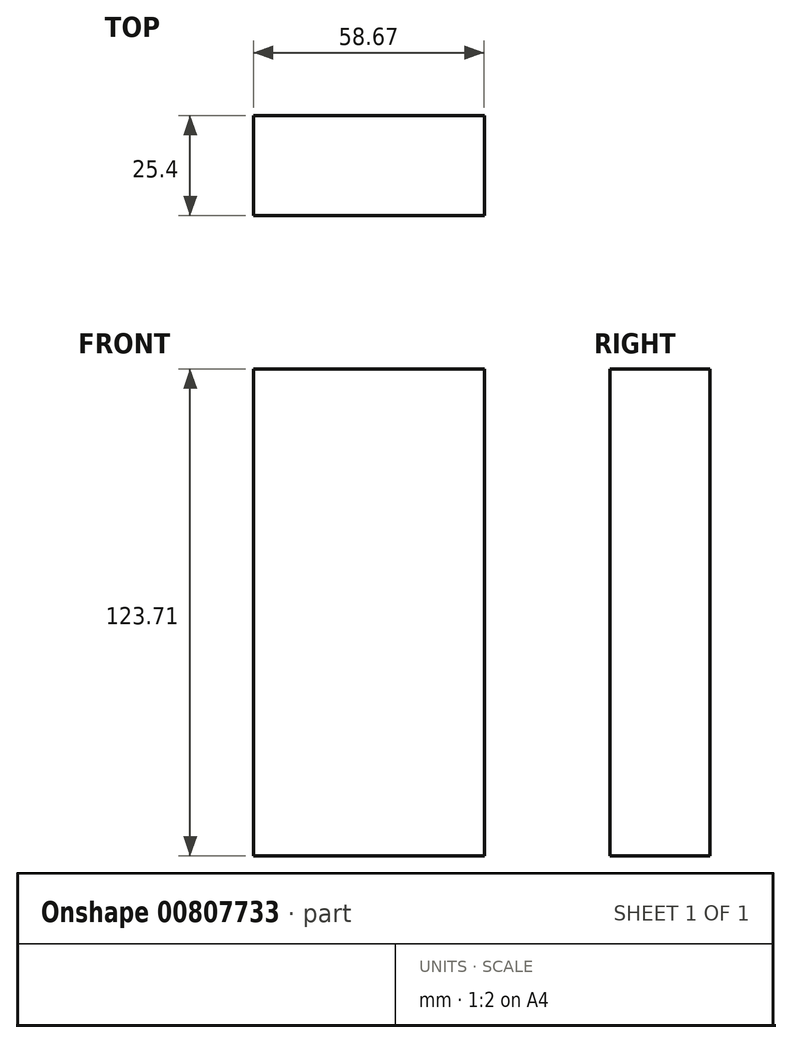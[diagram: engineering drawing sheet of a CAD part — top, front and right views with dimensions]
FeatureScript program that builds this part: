
annotation { "Feature Type Name" : "Feature", "Feature Type Description" : "" }
export const myFeature = defineFeature(function(context is Context, id is Id, definition is map)
    precondition{}
    {
        {
            var Q0;
            Q0=qCreatedBy(makeId("Front.planeOp"),FACE);
            var sketch = newSketch(context, id + "F0", { "sketchPlane" : qUnion([Q0])});
            skLineSegment(sketch, "E0", {"start": v(0, 141.53) * mm, "end": v(0, 17.83) * mm});
            skLineSegment(sketch, "E1", {"start": v(0, 141.53) * mm, "end": v(58.67, 141.53) * mm});
            skLineSegment(sketch, "E2", {"start": v(58.67, 141.53) * mm, "end": v(58.67, 17.82) * mm});
            skLineSegment(sketch, "E3", {"start": v(0, 17.83) * mm, "end": v(58.67, 17.82) * mm});
            skSolve(sketch);
        }
        {
            var Q0;
            Q0=makeQuery(id+"F0.imprint","IMPRINT",FACE,{"disambiguationData":[TD([[makeQuery(id+"F0.imprint","IMPRINT",EDGE,{"derivedFrom":sQuery(id+"F0.wireOp",EDGE,"E0")}),1.0]])]});
            extrude(context, id + "F1", {"entities" : qUnion([Q0]), "depth" : 25.4 * mm, "offsetDistance" : 25.4 * mm});
        }
    });
